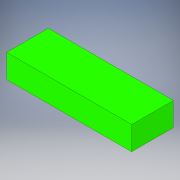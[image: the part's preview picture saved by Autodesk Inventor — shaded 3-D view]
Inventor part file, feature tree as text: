
AUTODESK INVENTOR PART (.ipt)
format: ipt  version: 2019 (Build 230136000, 136)  size: 97,792 bytes
history: native  units: mm
features: extrude x1, sketch x1
ambient origin geometry x8: Origin, YZ Plane, XZ Plane, XY Plane, X Axis, Y Axis, Z Axis, Center Point
bodies: Solid1 (feature_tree)
feature tree (2):
  extrude  "Extrusion1"  Depth=46.0mm
  sketch  "Sketch1"  dims[d0=138.0mm d1=46.0mm d2=26.0mm d3=0.0mm]
